# Revit family: v-122bz5_60Hz
name_source: partatom
category: 機械設備
units: mm (PartAtom-declared; Revit-internal decimal feet)

## family parameters
OmniClass タイトル = Centrifugal Fans
OmniClass 番号 = 23.75.35.17.27
パーツ タイプ = 標準
ロード時にボイドで切り取り = いいえ
丸型コネクタ寸法 = 直径を使用
作業面ベース = いいえ
共有 = いいえ
常に垂直 = はい
部屋計算ポイント = はい

## types (1)
- V-122BZ5
    D1 = 495  [stored 1.62402 ft]
    Depth = 400  [stored 1.31234 ft]
    Duct_Depth = 61  [stored 0.200131 ft]
    Duct_EA_W = 133  [stored 0.436352 ft]
    Duct_H = 95
    Duct_RA_W1 = 21  [stored 0.0688976 ft]
    Duct_RA_W2 = 76
    Duct_RA_W3 = 21  [stored 0.0688976 ft]
    EAサイズ_D = 98  [stored 0.321522 ft]
    H1 = 40  [stored 0.131234 ft]
    Height = 200  [stored 0.656168 ft]
    IfcExportAs = IfcFanType
    IfcExportType = PROPELLORAXIAL
    MAX静圧 = 0.0 Pa
    MAX風量 = 200.0 m³/h
    MID静圧 = 0.0 Pa
    MID風量 = 0.0 m³/h
    MIN静圧 = 0.0 Pa
    MIN風量 = 105.0 m³/h
    OmniClassCode = 23-33 31 19 11 15
    RAサイズ_D = 98  [stored 0.321522 ft]
    RAダクト接続口_A = はい
    RAダクト接続口_B = いいえ
    RAダクト接続口_C = いいえ
    URL = https://www.mitsubishielectric.co.jp
    Uniclass2015Code = Pr_65_67_29_12
    Uniclass2015Title = Centrifugal fans
    Uniclass2015Version = Systems v1.9
    W1 = 490  [stored 1.60761 ft]
    Width = 400  [stored 1.31234 ft]
    カバーマテリアル = 合成樹脂(白)
    ダクト径 = 100 mm
    マテリアル = 亜鉛メッキ鋼板
    モデル = V-122BZ5
    仕様書バージョン = Version1.0
    企業コード = 108420
    価格 = 124600 $
    分類コード = 50052503100080
    周波数 = 60 Hz
    呼称 = 天井扇
    天吊金具_径 = 15  [stored 0.0492126 ft]
    天吊金具_高さ = 98  [stored 0.321522 ft]
    天吊金具ピッチ1 = 448  [stored 1.46982 ft]
    天吊金具ピッチ2 = 354  [stored 1.16142 ft]
    極数 = 2
    法定耐用年数 = 10
    消費電力 = 1230 W
    点検口 = はい
    点検口_Depth = 450  [stored 1.47638 ft]
    点検口離隔 = 150
    相 = 1
    積算_科目 = 2 換気設備
    製品リリース年月 = 2022年6月1日
    製品出荷対象 = 国内
    製品質量 = 10.00 kg
    製造元 = 三菱電機株式会社
    設置方法 = カセット形
    説明 = バス乾燥・暖房・換気システム 従来タイプ取替専用
    負荷分類 = 3_ファン類
    質量 = 12.00 kg
    運転質量 = 0.00 kg
    電動機出力 = 0 W
    電圧 = 100 V

note: [stored X ft] marks values corroborated as IEEE doubles in the binary element streams (Revit-internal decimal feet)
